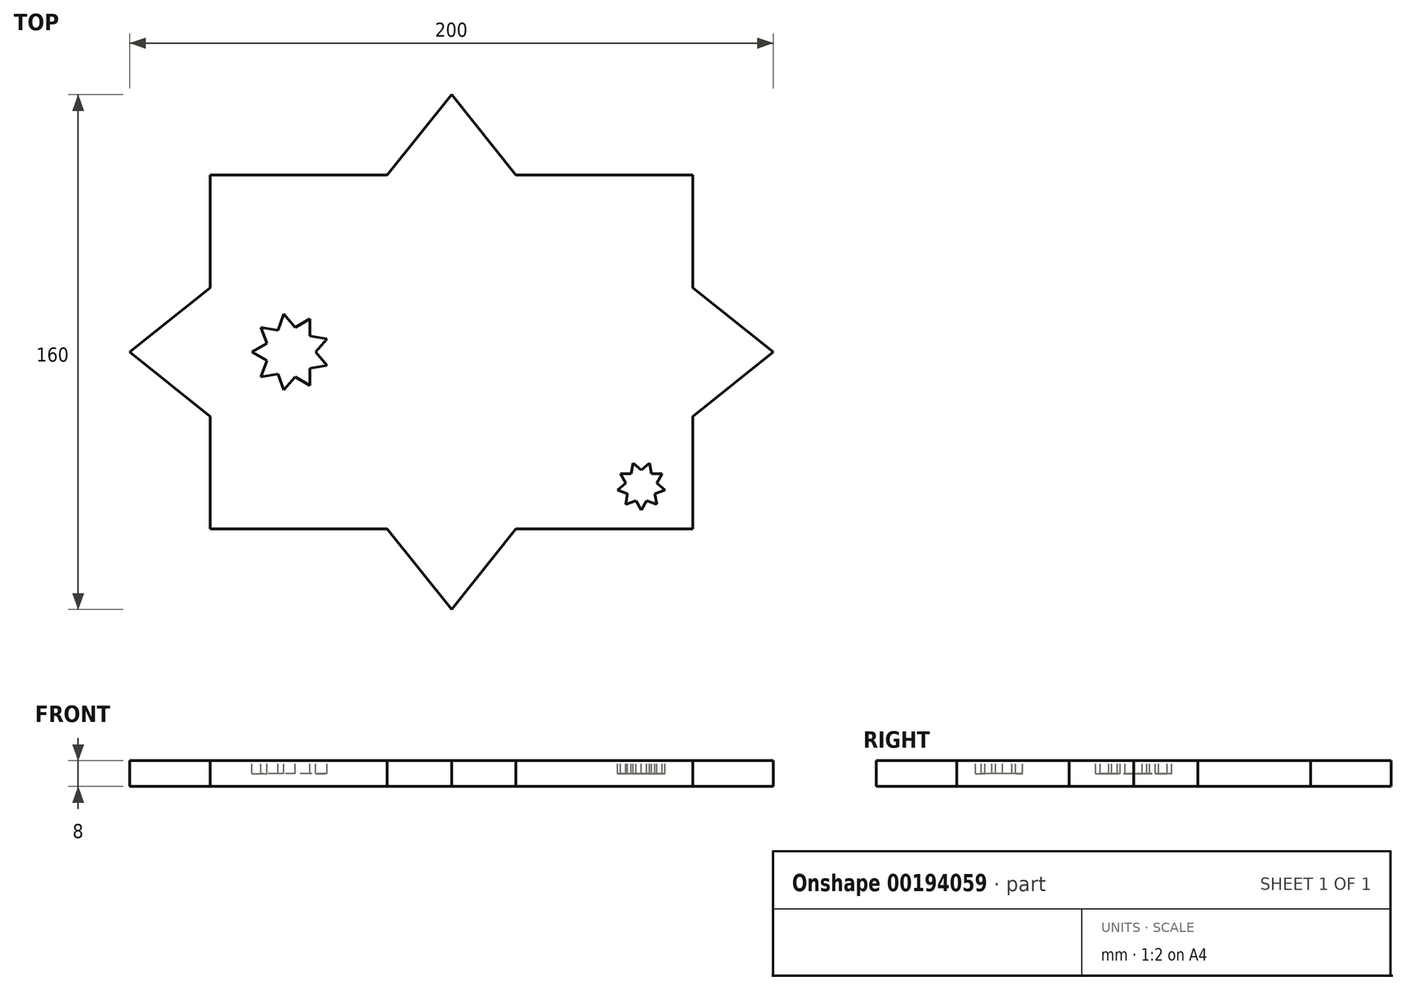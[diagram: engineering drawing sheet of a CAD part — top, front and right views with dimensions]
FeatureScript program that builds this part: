
annotation { "Feature Type Name" : "Feature", "Feature Type Description" : "" }
export const myFeature = defineFeature(function(context is Context, id is Id, definition is map)
    precondition{}
    {
        {
            var Q0;
            Q0=qCreatedBy(makeId("Top.planeOp"),FACE);
            var sketch = newSketch(context, id + "F0", { "sketchPlane" : qUnion([Q0])});
            skLineSegment(sketch, "E0.bottom", {"start": v(75, 55) * mm, "end": v(20, 55) * mm});
            skLineSegment(sketch, "E0.top", {"start": v(75, -55) * mm, "end": v(20, -55) * mm});
            skLineSegment(sketch, "E0.left", {"start": v(75, 55) * mm, "end": v(75, 20) * mm});
            skLineSegment(sketch, "E0.right", {"start": v(-75, 55) * mm, "end": v(-75, 20) * mm});
            skLineSegment(sketch, "E1", {"start": v(75, 20) * mm, "end": v(100, 0) * mm});
            skLineSegment(sketch, "E2", {"start": v(-20, 55) * mm, "end": v(0, 80) * mm});
            skLineSegment(sketch, "E3", {"start": v(0, 80) * mm, "end": v(20, 55) * mm});
            skLineSegment(sketch, "E4.MirrorCS", {"start": v(-20, -55) * mm, "end": v(0, -80) * mm});
            skLineSegment(sketch, "E5.MirrorCS", {"start": v(0, -80) * mm, "end": v(20, -55) * mm});
            skLineSegment(sketch, "E6.MirrorCS", {"start": v(75, -20) * mm, "end": v(100, 0) * mm});
            skLineSegment(sketch, "E7.MirrorCS", {"start": v(-75, 20) * mm, "end": v(-100, 0) * mm});
            skLineSegment(sketch, "E8.MirrorCS", {"start": v(-75, -20) * mm, "end": v(-100, 0) * mm});
            skLineSegment(sketch, "E9.trimOffspring", {"start": v(-75, -20) * mm, "end": v(-75, -55) * mm});
            skLineSegment(sketch, "E10.trimOffspring", {"start": v(75, -20) * mm, "end": v(75, -55) * mm});
            skLineSegment(sketch, "E11.trimOffspring", {"start": v(-20, -55) * mm, "end": v(-75, -55) * mm});
            skLineSegment(sketch, "E12.trimOffspring", {"start": v(-20, 55) * mm, "end": v(-75, 55) * mm});
            skPoint(sketch, "E13.MirrorCS.end.orphan", {"position": v(75, 34.57) * mm});
            skPoint(sketch, "E13.MirrorCS.start.orphan", {"position": v(100, 0) * mm});
            skPoint(sketch, "E14.orphan", {"position": v(75, -34.57) * mm});
            skSolve(sketch);
        }
        {
            var Q0;
            Q0=qSketchRegion(id+"F0",true);
            extrude(context, id + "F1", {"entities" : qUnion([Q0]), "depth" : 3 * mm});
        }
        {
            var Q0;
            Q0=makeQuery(id+"F1.opExtrude","CAP_FACE",FACE,{"disambiguationData":[OSD([sQuery(id+"F0.wireOp",EDGE,"E0.bottom"),sQuery(id+"F0.wireOp",EDGE,"E0.top"),sQuery(id+"F0.wireOp",EDGE,"E0.left"),sQuery(id+"F0.wireOp",EDGE,"E0.right"),sQuery(id+"F0.wireOp",EDGE,"b7ca5f3b-2874-41bd-b902-1c79f96a0a8620.MirrorC"),sQuery(id+"F0.wireOp",EDGE,"b7ca5f3b-2874-41bd-b902-1c79f96a0a8621.MirrorC"),sQuery(id+"F0.wireOp",EDGE,"b7ca5f3b-2874-41bd-b902-1c79f96a0a8622.MirrorCS"),sQuery(id+"F0.wireOp",EDGE,"b7ca5f3b-2874-41bd-b902-1c79f96a0a8623.MirrorCS"),sQuery(id+"F0.wireOp",EDGE,"b7ca5f3b-2874-41bd-b902-1c79f96a0a8624.MirrorCS"),sQuery(id+"F0.wireOp",EDGE,"b7ca5f3b-2874-41bd-b902-1c79f96a0a8625.MirrorCS"),sQuery(id+"F0.wireOp",EDGE,"70034771-ba44-435e-ab74-29499f25fa1546.MirrorC"),sQuery(id+"F0.wireOp",EDGE,"70034771-ba44-435e-ab74-29499f25fa1547.MirrorCS"),sQuery(id+"F0.wireOp",EDGE,"70034771-ba44-435e-ab74-29499f25fa1548.MirrorC"),sQuery(id+"F0.wireOp",EDGE,"70034771-ba44-435e-ab74-29499f25fa1549.MirrorCS"),sQuery(id+"F0.wireOp",EDGE,"70034771-ba44-435e-ab74-29499f25fa1550.MirrorCS"),sQuery(id+"F0.wireOp",EDGE,"70034771-ba44-435e-ab74-29499f25fa1551.MirrorCS"),sQuery(id+"F0.wireOp",EDGE,"E1"),sQuery(id+"F0.wireOp",EDGE,"E2"),sQuery(id+"F0.wireOp",EDGE,"E3"),sQuery(id+"F0.wireOp",EDGE,"E4.MirrorCS"),sQuery(id+"F0.wireOp",EDGE,"E5.MirrorCS"),sQuery(id+"F0.wireOp",EDGE,"E6.MirrorCS"),sQuery(id+"F0.wireOp",EDGE,"E7.MirrorCS"),sQuery(id+"F0.wireOp",EDGE,"E8.MirrorCS"),sQuery(id+"F0.wireOp",EDGE,"E9.trimOffspring"),sQuery(id+"F0.wireOp",EDGE,"E10.trimOffspring"),sQuery(id+"F0.wireOp",EDGE,"E11.trimOffspring"),sQuery(id+"F0.wireOp",EDGE,"E12.trimOffspring")])],"isStart":false});
            var sketch = newSketch(context, id + "F2", { "sketchPlane" : qUnion([Q0])});
            skLineSegment(sketch, "E15.1.0", {"start": v(-59.2, -7.71) * mm, "end": v(-57.36, -2.68) * mm});
            skLineSegment(sketch, "E15.1.1", {"start": v(-59.2, 7.71) * mm, "end": v(-53.92, 6.78) * mm});
            skLineSegment(sketch, "E15.1.2", {"start": v(-48.64, 7.71) * mm, "end": v(-44, 10.4) * mm});
            skPoint(sketch, "E15.1.3", {"position": v(-55.64, -2.05) * mm});
            skLineSegment(sketch, "E15.1.4", {"start": v(-52.08, -11.82) * mm, "end": v(-53.92, -6.78) * mm});
            skLineSegment(sketch, "E15.1.5", {"start": v(-44, -5.03) * mm, "end": v(-44, -10.4) * mm});
            skArc(sketch, "E15.1.6", {"start": v(-48.96, 5.9) * mm, "mid": v(-54.6, -3.86) * mm, "end": v(-44, 0) * mm, "construction": true});
            skLineSegment(sketch, "E15.1.7", {"start": v(-53.92, 6.78) * mm, "end": v(-52.08, 11.82) * mm});
            skPoint(sketch, "E15.1.8", {"position": v(-53, -5.2) * mm});
            skLineSegment(sketch, "E15.1.9", {"start": v(-44, 10.4) * mm, "end": v(-44, 5.03) * mm});
            skLineSegment(sketch, "E15.1.10", {"start": v(-48.64, -7.71) * mm, "end": v(-52.08, -11.82) * mm});
            skLineSegment(sketch, "E15.1.11", {"start": v(-44, -10.4) * mm, "end": v(-48.64, -7.71) * mm});
            skCircle(sketch, "E15.1.12", {"center": v(-50, 0) * mm, "radius": 6 * mm, "construction": true});
            skLineSegment(sketch, "E15.1.13", {"start": v(-38.72, -4.1) * mm, "end": v(-44, -5.03) * mm});
            skLineSegment(sketch, "E15.1.14", {"start": v(-44, 5.03) * mm, "end": v(-38.72, 4.1) * mm});
            skLineSegment(sketch, "E15.1.15", {"start": v(-57.36, 2.68) * mm, "end": v(-59.2, 7.71) * mm});
            skLineSegment(sketch, "E15.1.16", {"start": v(-42.17, 0) * mm, "end": v(-38.72, -4.1) * mm});
            skLineSegment(sketch, "E15.1.17", {"start": v(-52.08, 11.82) * mm, "end": v(-48.64, 7.71) * mm});
            skPoint(sketch, "E15.1.18", {"position": v(-55.64, 2.05) * mm});
            skArc(sketch, "E15.1.19", {"start": v(-55.64, 2.05) * mm, "mid": v(-56, 0) * mm, "end": v(-55.64, -2.05) * mm, "construction": true});
            skArc(sketch, "E15.1.20", {"start": v(-53, -5.2) * mm, "mid": v(-44, 0) * mm, "end": v(-53, 5.2) * mm, "construction": true});
            skLineSegment(sketch, "E15.1.21", {"start": v(-62, 0) * mm, "end": v(-57.36, 2.68) * mm});
            skLineSegment(sketch, "E15.1.22", {"start": v(-53.92, -6.78) * mm, "end": v(-59.2, -7.71) * mm});
            skLineSegment(sketch, "E15.1.23", {"start": v(-57.36, -2.68) * mm, "end": v(-62, 0) * mm});
            skLineSegment(sketch, "E15.1.24", {"start": v(-38.72, 4.1) * mm, "end": v(-42.17, 0) * mm});
            skLineSegment(sketch, "E16.1.17", {"start": v(-32.89, -53.98) * mm, "end": v(-68.5, -53.98) * mm, "construction": true});
            skLineSegment(sketch, "E16.2.0", {"start": v(63.8, -40.7) * mm, "end": v(66.36, -42.86) * mm});
            skLineSegment(sketch, "E16.2.1", {"start": v(57.3, -46.15) * mm, "end": v(54.15, -47.3) * mm});
            skPoint(sketch, "E16.2.2", {"position": v(57.7, -45.08) * mm});
            skCircle(sketch, "E16.2.3", {"center": v(58.97, -41.55) * mm, "radius": 3.75 * mm, "construction": true});
            skLineSegment(sketch, "E16.2.4", {"start": v(51.59, -42.86) * mm, "end": v(54.15, -40.7) * mm});
            skLineSegment(sketch, "E16.2.5", {"start": v(63.8, -47.3) * mm, "end": v(60.65, -46.15) * mm});
            skLineSegment(sketch, "E16.2.6", {"start": v(60.65, -46.15) * mm, "end": v(58.97, -49.05) * mm});
            skLineSegment(sketch, "E16.2.7", {"start": v(65.47, -37.8) * mm, "end": v(63.8, -40.7) * mm});
            skLineSegment(sketch, "E16.2.9", {"start": v(52.48, -37.8) * mm, "end": v(55.83, -37.8) * mm});
            skLineSegment(sketch, "E16.2.10", {"start": v(56.4, -34.5) * mm, "end": v(58.97, -36.66) * mm});
            skLineSegment(sketch, "E16.2.11", {"start": v(55.83, -37.8) * mm, "end": v(56.4, -34.5) * mm});
            skLineSegment(sketch, "E16.2.12", {"start": v(66.36, -42.86) * mm, "end": v(63.21, -44) * mm});
            skLineSegment(sketch, "E16.2.13", {"start": v(54.15, -47.3) * mm, "end": v(54.73, -44) * mm});
            skLineSegment(sketch, "E16.2.14", {"start": v(54.15, -40.7) * mm, "end": v(52.48, -37.8) * mm});
            skLineSegment(sketch, "E16.2.15", {"start": v(54.73, -44) * mm, "end": v(51.59, -42.86) * mm});
            skPoint(sketch, "E16.2.16", {"position": v(62.22, -43.43) * mm});
            skPoint(sketch, "E16.2.18", {"position": v(60.26, -45.08) * mm});
            skLineSegment(sketch, "E16.2.19", {"start": v(58.97, -49.05) * mm, "end": v(57.3, -46.15) * mm});
            skLineSegment(sketch, "E16.2.20", {"start": v(58.97, -36.66) * mm, "end": v(61.54, -34.5) * mm});
            skLineSegment(sketch, "E16.2.21", {"start": v(63.21, -44) * mm, "end": v(63.8, -47.3) * mm});
            skLineSegment(sketch, "E16.2.22", {"start": v(61.54, -34.5) * mm, "end": v(62.12, -37.8) * mm});
            skLineSegment(sketch, "E16.2.23", {"start": v(62.12, -37.8) * mm, "end": v(65.47, -37.8) * mm});
            skArc(sketch, "E16.2.24", {"start": v(62.22, -43.43) * mm, "mid": v(59.65, -37.86) * mm, "end": v(55.27, -42.16) * mm, "construction": true});
            skArc(sketch, "E16.2.25", {"start": v(57.7, -45.08) * mm, "mid": v(58.97, -45.3) * mm, "end": v(60.26, -45.08) * mm, "construction": true});
            skArc(sketch, "E16.2.26", {"start": v(51.1, -40.25) * mm, "mid": v(66.62, -43.82) * mm, "end": v(51.66, -38.37) * mm, "construction": true});
            skSolve(sketch);
        }
        {
            var Q0;
            Q0=qSketchRegion(id+"F2",true);
            extrude(context, id + "F3", {"entities" : qUnion([Q0]), "operationType" : NewBodyOperationType.REMOVE, "oppositeDirection" : true, "depth" : 25 * mm});
        }
        {
            var Q0;
            Q0=makeQuery(id+"F1.opExtrude","CAP_FACE",FACE,{"disambiguationData":[OSD([sQuery(id+"F0.wireOp",EDGE,"E0.bottom"),sQuery(id+"F0.wireOp",EDGE,"E0.top"),sQuery(id+"F0.wireOp",EDGE,"E0.left"),sQuery(id+"F0.wireOp",EDGE,"E0.right"),sQuery(id+"F0.wireOp",EDGE,"b7ca5f3b-2874-41bd-b902-1c79f96a0a8620.MirrorC"),sQuery(id+"F0.wireOp",EDGE,"b7ca5f3b-2874-41bd-b902-1c79f96a0a8621.MirrorC"),sQuery(id+"F0.wireOp",EDGE,"b7ca5f3b-2874-41bd-b902-1c79f96a0a8622.MirrorCS"),sQuery(id+"F0.wireOp",EDGE,"b7ca5f3b-2874-41bd-b902-1c79f96a0a8623.MirrorCS"),sQuery(id+"F0.wireOp",EDGE,"b7ca5f3b-2874-41bd-b902-1c79f96a0a8624.MirrorCS"),sQuery(id+"F0.wireOp",EDGE,"b7ca5f3b-2874-41bd-b902-1c79f96a0a8625.MirrorCS"),sQuery(id+"F0.wireOp",EDGE,"70034771-ba44-435e-ab74-29499f25fa1546.MirrorC"),sQuery(id+"F0.wireOp",EDGE,"70034771-ba44-435e-ab74-29499f25fa1547.MirrorCS"),sQuery(id+"F0.wireOp",EDGE,"70034771-ba44-435e-ab74-29499f25fa1548.MirrorC"),sQuery(id+"F0.wireOp",EDGE,"70034771-ba44-435e-ab74-29499f25fa1549.MirrorCS"),sQuery(id+"F0.wireOp",EDGE,"70034771-ba44-435e-ab74-29499f25fa1550.MirrorCS"),sQuery(id+"F0.wireOp",EDGE,"70034771-ba44-435e-ab74-29499f25fa1551.MirrorCS"),sQuery(id+"F0.wireOp",EDGE,"E1"),sQuery(id+"F0.wireOp",EDGE,"E2"),sQuery(id+"F0.wireOp",EDGE,"E3"),sQuery(id+"F0.wireOp",EDGE,"E4.MirrorCS"),sQuery(id+"F0.wireOp",EDGE,"E5.MirrorCS"),sQuery(id+"F0.wireOp",EDGE,"E6.MirrorCS"),sQuery(id+"F0.wireOp",EDGE,"E7.MirrorCS"),sQuery(id+"F0.wireOp",EDGE,"E8.MirrorCS"),sQuery(id+"F0.wireOp",EDGE,"E9.trimOffspring"),sQuery(id+"F0.wireOp",EDGE,"E10.trimOffspring"),sQuery(id+"F0.wireOp",EDGE,"E11.trimOffspring"),sQuery(id+"F0.wireOp",EDGE,"E12.trimOffspring")])],"isStart":true});
            var sketch = newSketch(context, id + "F4", { "sketchPlane" : qUnion([Q0])});
            skLineSegment(sketch, "E17.0", {"start": v(-20, 55) * mm, "end": v(-75, 55) * mm});
            skLineSegment(sketch, "E18.0", {"start": v(-20, 55) * mm, "end": v(0, 80) * mm});
            skLineSegment(sketch, "E19.0", {"start": v(0, 80) * mm, "end": v(20, 55) * mm});
            skLineSegment(sketch, "E20.0", {"start": v(75, 55) * mm, "end": v(20, 55) * mm});
            skPoint(sketch, "E21.0", {"position": v(75, 37.5) * mm});
            skLineSegment(sketch, "E22.0", {"start": v(75, 20) * mm, "end": v(75, 55) * mm});
            skLineSegment(sketch, "E23.0", {"start": v(75, 20) * mm, "end": v(100, 0) * mm});
            skLineSegment(sketch, "E24.0", {"start": v(75, -20) * mm, "end": v(100, 0) * mm});
            skLineSegment(sketch, "E25.0", {"start": v(75, -55) * mm, "end": v(75, -20) * mm});
            skLineSegment(sketch, "E26.0", {"start": v(75, -55) * mm, "end": v(20, -55) * mm});
            skLineSegment(sketch, "E27.0", {"start": v(0, -80) * mm, "end": v(20, -55) * mm});
            skLineSegment(sketch, "E28.0", {"start": v(-20, -55) * mm, "end": v(0, -80) * mm});
            skLineSegment(sketch, "E29.0", {"start": v(-20, -55) * mm, "end": v(-75, -55) * mm});
            skLineSegment(sketch, "E30.0", {"start": v(-75, -55) * mm, "end": v(-75, -20) * mm});
            skLineSegment(sketch, "E31.0", {"start": v(-75, -20) * mm, "end": v(-100, 0) * mm});
            skLineSegment(sketch, "E32.0", {"start": v(-75, 20) * mm, "end": v(-100, 0) * mm});
            skLineSegment(sketch, "E33.0", {"start": v(-75, 20) * mm, "end": v(-75, 55) * mm});
            skSolve(sketch);
        }
        {
            var Q0;
            Q0=qSketchRegion(id+"F4",true);
            extrude(context, id + "F5", {"entities" : qUnion([Q0]), "operationType" : NewBodyOperationType.ADD, "depth" : 5 * mm});
        }
        {
            var Q0;
            Q0=qCreatedBy(makeId("Right.planeOp"),FACE);
            var sketch = newSketch(context, id + "F6", { "sketchPlane" : qUnion([Q0])});
            skLineSegment(sketch, "E34", {"start": v(0, -70.92) * mm, "end": v(0, 69.35) * mm, "construction": true});
            skSolve(sketch);
        }
        {
            var Q0;
            Q0=makeQuery(id+"F1.opExtrude","CAP_FACE",FACE,{"disambiguationData":[OSD([sQuery(id+"F0.wireOp",EDGE,"E0.bottom"),sQuery(id+"F0.wireOp",EDGE,"E0.top"),sQuery(id+"F0.wireOp",EDGE,"E0.left"),sQuery(id+"F0.wireOp",EDGE,"E0.right"),sQuery(id+"F0.wireOp",EDGE,"E1"),sQuery(id+"F0.wireOp",EDGE,"E2"),sQuery(id+"F0.wireOp",EDGE,"E3"),sQuery(id+"F0.wireOp",EDGE,"E4.MirrorCS"),sQuery(id+"F0.wireOp",EDGE,"E5.MirrorCS"),sQuery(id+"F0.wireOp",EDGE,"E6.MirrorCS"),sQuery(id+"F0.wireOp",EDGE,"E7.MirrorCS"),sQuery(id+"F0.wireOp",EDGE,"E8.MirrorCS"),sQuery(id+"F0.wireOp",EDGE,"E9.trimOffspring"),sQuery(id+"F0.wireOp",EDGE,"E10.trimOffspring"),sQuery(id+"F0.wireOp",EDGE,"E11.trimOffspring"),sQuery(id+"F0.wireOp",EDGE,"E12.trimOffspring")])],"isStart":false});
            var sketch = newSketch(context, id + "F7", { "sketchPlane" : qUnion([Q0])});
            skLineSegment(sketch, "E35.0", {"start": v(-38.72, -4.1) * mm, "end": v(-44, -5.03) * mm});
            skLineSegment(sketch, "E36.0", {"start": v(-42.17, 0) * mm, "end": v(-38.72, -4.1) * mm});
            skLineSegment(sketch, "E37.0", {"start": v(-38.72, 4.1) * mm, "end": v(-42.17, 0) * mm});
            skLineSegment(sketch, "E38.0", {"start": v(-44, 5.03) * mm, "end": v(-38.72, 4.1) * mm});
            skLineSegment(sketch, "E39.0", {"start": v(-44, 10.4) * mm, "end": v(-44, 5.03) * mm});
            skLineSegment(sketch, "E40.0", {"start": v(-48.64, 7.71) * mm, "end": v(-44, 10.4) * mm});
            skLineSegment(sketch, "E41.0", {"start": v(-52.08, 11.82) * mm, "end": v(-48.64, 7.71) * mm});
            skLineSegment(sketch, "E42.0", {"start": v(-53.92, 6.78) * mm, "end": v(-52.08, 11.82) * mm});
            skLineSegment(sketch, "E43.0", {"start": v(-59.2, 7.71) * mm, "end": v(-53.92, 6.78) * mm});
            skLineSegment(sketch, "E44.0", {"start": v(-62, 0) * mm, "end": v(-57.36, 2.68) * mm});
            skLineSegment(sketch, "E45.0", {"start": v(-57.36, -2.68) * mm, "end": v(-62, 0) * mm});
            skLineSegment(sketch, "E46.0", {"start": v(-59.2, -7.71) * mm, "end": v(-57.36, -2.68) * mm});
            skLineSegment(sketch, "E47.0", {"start": v(-53.92, -6.78) * mm, "end": v(-59.2, -7.71) * mm});
            skLineSegment(sketch, "E48.0", {"start": v(-52.08, -11.82) * mm, "end": v(-53.92, -6.78) * mm});
            skLineSegment(sketch, "E49.0", {"start": v(-48.64, -7.71) * mm, "end": v(-52.08, -11.82) * mm});
            skLineSegment(sketch, "E50.0", {"start": v(-44, -10.4) * mm, "end": v(-48.64, -7.71) * mm});
            skLineSegment(sketch, "E51.0", {"start": v(-44, -5.03) * mm, "end": v(-44, -10.4) * mm});
            skLineSegment(sketch, "E52.0", {"start": v(-57.36, 2.68) * mm, "end": v(-59.2, 7.71) * mm});
            skSolve(sketch);
        }
        {
            var Q0;
            Q0 = qSketchRegion(id + "F7", true);
            extrude(context, id + "F8", {"entities" : qUnion([Q0]), "operationType" : NewBodyOperationType.REMOVE, "oppositeDirection" : true, "depth" : 4 * mm});
        }
        {
            var Q0;
            Q0=makeQuery(id+"F1.opExtrude","CAP_FACE",FACE,{"disambiguationData":[OSD([sQuery(id+"F0.wireOp",EDGE,"E0.bottom"),sQuery(id+"F0.wireOp",EDGE,"E0.top"),sQuery(id+"F0.wireOp",EDGE,"E0.left"),sQuery(id+"F0.wireOp",EDGE,"E0.right"),sQuery(id+"F0.wireOp",EDGE,"E1"),sQuery(id+"F0.wireOp",EDGE,"E2"),sQuery(id+"F0.wireOp",EDGE,"E3"),sQuery(id+"F0.wireOp",EDGE,"E4.MirrorCS"),sQuery(id+"F0.wireOp",EDGE,"E5.MirrorCS"),sQuery(id+"F0.wireOp",EDGE,"E6.MirrorCS"),sQuery(id+"F0.wireOp",EDGE,"E7.MirrorCS"),sQuery(id+"F0.wireOp",EDGE,"E8.MirrorCS"),sQuery(id+"F0.wireOp",EDGE,"E9.trimOffspring"),sQuery(id+"F0.wireOp",EDGE,"E10.trimOffspring"),sQuery(id+"F0.wireOp",EDGE,"E11.trimOffspring"),sQuery(id+"F0.wireOp",EDGE,"E12.trimOffspring")])],"isStart":false});
            var sketch = newSketch(context, id + "F9", { "sketchPlane" : qUnion([Q0])});
            skLineSegment(sketch, "E53.0", {"start": v(63.8, -47.3) * mm, "end": v(60.65, -46.15) * mm});
            skLineSegment(sketch, "E54.0", {"start": v(63.21, -44) * mm, "end": v(63.8, -47.3) * mm});
            skLineSegment(sketch, "E55.0.0", {"start": v(-75, -55) * mm, "end": v(-20, -55) * mm});
            skLineSegment(sketch, "E55.0.1", {"start": v(-20, -55) * mm, "end": v(0, -80) * mm});
            skLineSegment(sketch, "E55.0.2", {"start": v(0, -80) * mm, "end": v(20, -55) * mm});
            skLineSegment(sketch, "E55.0.3", {"start": v(20, -55) * mm, "end": v(75, -55) * mm});
            skLineSegment(sketch, "E55.0.4", {"start": v(75, -55) * mm, "end": v(75, -20) * mm});
            skLineSegment(sketch, "E55.0.5", {"start": v(75, -20) * mm, "end": v(100, 0) * mm});
            skLineSegment(sketch, "E55.0.6", {"start": v(100, 0) * mm, "end": v(75, 20) * mm});
            skLineSegment(sketch, "E55.0.7", {"start": v(75, 20) * mm, "end": v(75, 55) * mm});
            skLineSegment(sketch, "E55.0.8", {"start": v(75, 55) * mm, "end": v(20, 55) * mm});
            skLineSegment(sketch, "E55.0.9", {"start": v(20, 55) * mm, "end": v(0, 80) * mm});
            skLineSegment(sketch, "E55.0.10", {"start": v(0, 80) * mm, "end": v(-20, 55) * mm});
            skLineSegment(sketch, "E55.0.11", {"start": v(-20, 55) * mm, "end": v(-75, 55) * mm});
            skLineSegment(sketch, "E55.0.12", {"start": v(-75, 55) * mm, "end": v(-75, 20) * mm});
            skLineSegment(sketch, "E55.0.13", {"start": v(-75, 20) * mm, "end": v(-100, 0) * mm});
            skLineSegment(sketch, "E55.0.14", {"start": v(-100, 0) * mm, "end": v(-75, -20) * mm});
            skLineSegment(sketch, "E55.0.15", {"start": v(-75, -20) * mm, "end": v(-75, -55) * mm});
            skLineSegment(sketch, "E56.0", {"start": v(63.8, -40.7) * mm, "end": v(66.36, -42.86) * mm});
            skLineSegment(sketch, "E57.0", {"start": v(65.47, -37.8) * mm, "end": v(63.8, -40.7) * mm});
            skLineSegment(sketch, "E58.0", {"start": v(62.12, -37.8) * mm, "end": v(65.47, -37.8) * mm});
            skLineSegment(sketch, "E59.0", {"start": v(61.54, -34.5) * mm, "end": v(62.12, -37.8) * mm});
            skLineSegment(sketch, "E60.0", {"start": v(58.97, -36.66) * mm, "end": v(61.54, -34.5) * mm});
            skLineSegment(sketch, "E61.0", {"start": v(56.4, -34.5) * mm, "end": v(58.97, -36.66) * mm});
            skLineSegment(sketch, "E62.0", {"start": v(55.83, -37.8) * mm, "end": v(56.4, -34.5) * mm});
            skLineSegment(sketch, "E63.0", {"start": v(52.48, -37.8) * mm, "end": v(55.83, -37.8) * mm});
            skLineSegment(sketch, "E64.0", {"start": v(54.15, -40.7) * mm, "end": v(52.48, -37.8) * mm});
            skLineSegment(sketch, "E65.0", {"start": v(51.59, -42.86) * mm, "end": v(54.15, -40.7) * mm});
            skLineSegment(sketch, "E66.0", {"start": v(54.73, -44) * mm, "end": v(51.59, -42.86) * mm});
            skLineSegment(sketch, "E67.0", {"start": v(54.15, -47.3) * mm, "end": v(54.73, -44) * mm});
            skLineSegment(sketch, "E68.0", {"start": v(57.3, -46.15) * mm, "end": v(54.15, -47.3) * mm});
            skLineSegment(sketch, "E69.0", {"start": v(58.97, -49.05) * mm, "end": v(57.3, -46.15) * mm});
            skSolve(sketch);
        }
        {
            var Q0;
            Q0=makeQuery(id+"F9.imprint","IMPRINT",FACE,{"disambiguationData":[TD([[makeQuery(id+"F9.imprint","IMPRINT",EDGE,{"derivedFrom":sQuery(id+"F9.wireOp",EDGE,"E53.0")}),-1.0]])]});
            extrude(context, id + "F10", {"entities" : qUnion([Q0]), "operationType" : NewBodyOperationType.REMOVE, "oppositeDirection" : true, "depth" : 4 * mm});
        }
    });
